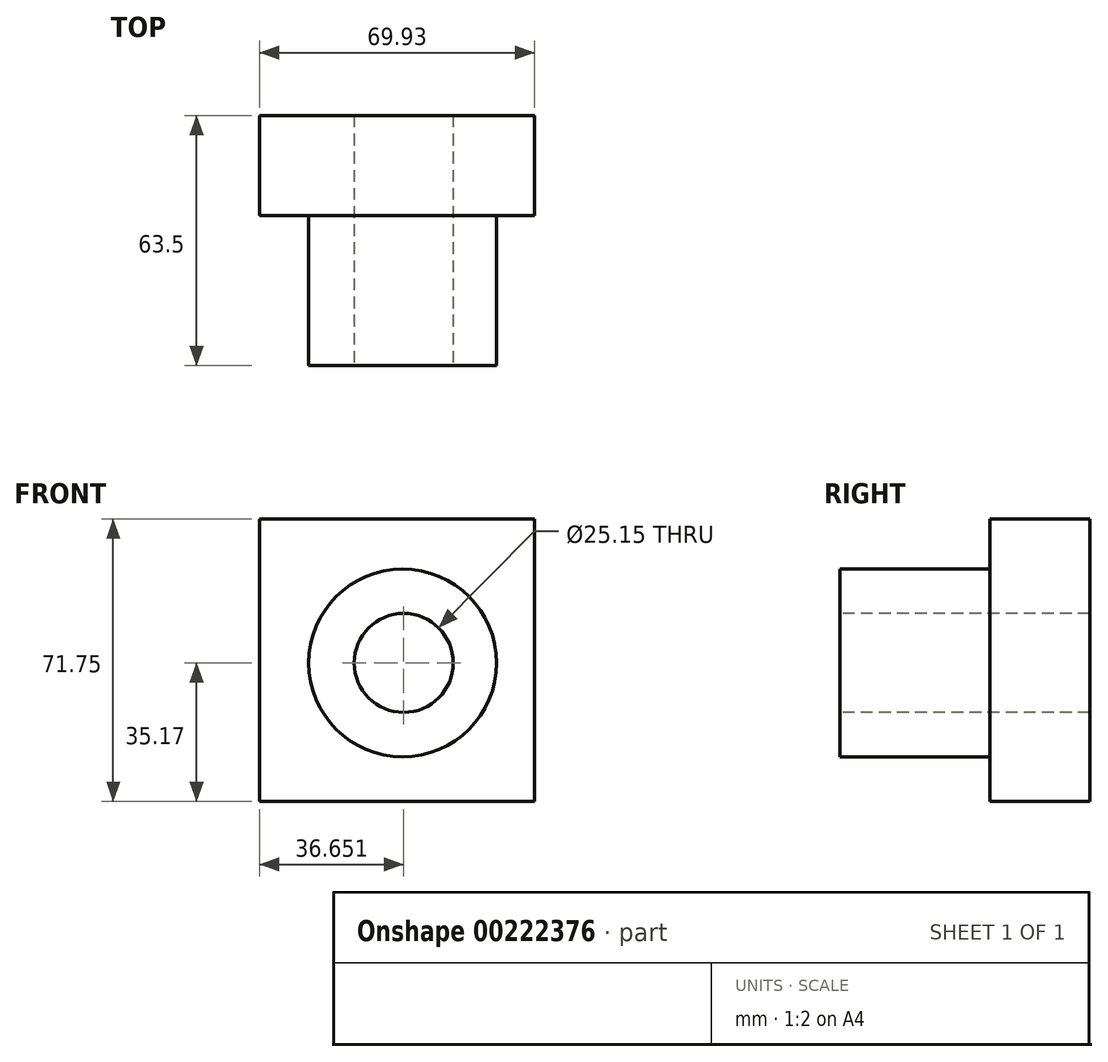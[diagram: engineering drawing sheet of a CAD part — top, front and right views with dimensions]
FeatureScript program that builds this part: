
annotation { "Feature Type Name" : "Feature", "Feature Type Description" : "" }
export const myFeature = defineFeature(function(context is Context, id is Id, definition is map)
    precondition{}
    {
        {
            var Q0;
            Q0=qCreatedBy(makeId("Front.planeOp"),FACE);
            var sketch = newSketch(context, id + "F0", { "sketchPlane" : qUnion([Q0])});
            skLineSegment(sketch, "E0.bottom", {"start": v(-31.8, 36.58) * mm, "end": v(38.12, 36.58) * mm});
            skLineSegment(sketch, "E0.top", {"start": v(-31.8, -35.17) * mm, "end": v(38.12, -35.17) * mm});
            skLineSegment(sketch, "E0.left", {"start": v(-31.8, 36.58) * mm, "end": v(-31.8, -35.17) * mm});
            skLineSegment(sketch, "E0.right", {"start": v(38.12, 36.58) * mm, "end": v(38.12, -35.17) * mm});
            skSolve(sketch);
        }
        {
            var Q0;
            Q0=makeQuery(id+"F0.imprint","IMPRINT",FACE,{"disambiguationData":[TD([[makeQuery(id+"F0.imprint","IMPRINT",EDGE,{"derivedFrom":sQuery(id+"F0.wireOp",EDGE,"E0.bottom")}),-1.0]])]});
            extrude(context, id + "F1", {"entities" : qUnion([Q0]), "depth" : 25.4 * mm});
        }
        {
            var Q0;
            Q0=makeQuery(id+"F1.opExtrude","CAP_FACE",FACE,{"disambiguationData":[OSD([sQuery(id+"F0.wireOp",EDGE,"E0.bottom"),sQuery(id+"F0.wireOp",EDGE,"E0.top"),sQuery(id+"F0.wireOp",EDGE,"E0.left"),sQuery(id+"F0.wireOp",EDGE,"E0.right")])],"isStart":false});
            var sketch = newSketch(context, id + "F3", { "sketchPlane" : qUnion([Q0])});
            skCircle(sketch, "E1", {"center": v(4.58, 0) * mm, "radius": 23.85 * mm});
            skSolve(sketch);
        }
        {
            var Q0;
            Q0=makeQuery(id+"F3.imprint","IMPRINT",FACE,{"disambiguationData":[TD([[makeQuery(id+"F3.imprint","IMPRINT",EDGE,{"derivedFrom":sQuery(id+"F3.wireOp",EDGE,"E1")}),1.0]])]});
            extrude(context, id + "F4", {"entities" : qUnion([Q0]), "operationType" : NewBodyOperationType.ADD, "depth" : 38.1 * mm});
        }
        {
            var Q0;
            Q0=makeQuery(id+"F4.opExtrude","CAP_FACE",FACE,{"disambiguationData":[OSD([sQuery(id+"F3.wireOp",EDGE,"E1")])],"isStart":false});
            var Q1;
            Q1=makeQuery(id+"F4.opExtrude","CAP_FACE",FACE,{"disambiguationData":[OSD([sQuery(id+"F3.wireOp",EDGE,"E1")])],"isStart":false});
            var sketch = newSketch(context, id + "F2", { "sketchPlane" : qUnion([Q0, Q1])});
            skSolve(sketch);
        }
        {
            var Q0;
            Q0=makeQuery(id+"F2.imprint","IMPRINT",FACE,{"disambiguationData":[TD([[makeQuery(id+"F2.imprint","IMPRINT",EDGE,{"derivedFrom":makeQuery(id+"F4.opExtrude","CAP_EDGE",EDGE,{"disambiguationData":[OSD([sQuery(id+"F3.wireOp",EDGE,"E1")])],"isStart":false})}),1.0]])]});
            var sketch = newSketch(context, id + "F5", { "sketchPlane" : qUnion([Q0])});
            skCircle(sketch, "E2", {"center": v(4.84, 0) * mm, "radius": 12.58 * mm});
            skSolve(sketch);
        }
        {
            var Q0;
            Q0=makeQuery(id+"F5.imprint","IMPRINT",FACE,{"disambiguationData":[TD([[makeQuery(id+"F5.imprint","IMPRINT",EDGE,{"derivedFrom":sQuery(id+"F5.wireOp",EDGE,"E2")}),1.0]])]});
            extrude(context, id + "F6", {"entities" : qUnion([Q0]), "operationType" : NewBodyOperationType.REMOVE, "endBound" : BoundingType.THROUGH_ALL, "oppositeDirection" : true, "depth" : 25.4 * mm});
        }
    });
